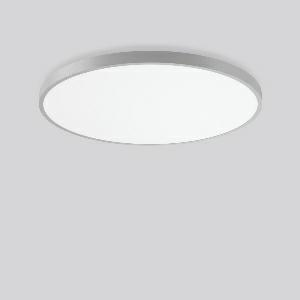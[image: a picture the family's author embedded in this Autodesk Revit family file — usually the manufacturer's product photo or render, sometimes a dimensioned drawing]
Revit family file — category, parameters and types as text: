
# Revit family: triona_round_a_312391_004_730_01d8
name_source: partatom
category: Lighting Fixtures
units: mm (PartAtom-declared; Revit-internal decimal feet)

## family parameters
Cut with Voids When Loaded = No
Host = Face
Light Source = No
Part Type = Normal
Room Calculation Point = No
Round Connector Dimension = Use Diameter
Shared = No

## types (1)
- TRIONA round A (1 x LED Modul 830, 11200 lm, 3000)
    Apparent Load = 106 VA
    CIE Flux Codes = 49 80 96 100 100
    Color Rendering = 80
    Color Temperature = 3000
    Default Elevation = 1800 mm
    Description = Series: TRIONA round
Decorative round LED surface-mounted luminaire. Flat, seamless frame: aluminium extrusion profile, powder coated. Cover made of sheet steel, powder-coated. Light emission through a diffuser: plastic, opal. Lightguide and diffuser made of non-yellowing plastic (PMMA). Lateral light emission (RZB SIDELITE technology) for above-average homogeneous light distribution. Suitable for Ceiling mounting, Wall (surface). Tool-free mounting via bayonet connection. Electronic ballast included. Very easy installation thanks to Plug+Play connection. With Casambi smart+free Bluetooth control for wireless network and operation using Android / iOS devices, free app available for download. 
Colour: silver, matt (approx. RAL 9006)
Diameter: 1009 mm
Height: 88 mm
Lamp: LED
Socket: without socket
Colour temperature: 3000K
Colour rendering index (CRI): 80
System power: 106 W
Rated luminous flux: 11200 lm
Luminous efficiency: 106 lm/W
Control gear: Dimmable Bluetooth converter
Protection class: I
Type of protection: IP 20
    Height = 88 mm
    Lamp = 1 x LED Modul 830
    Lamp Light Flux = 11200 lm
    Lamp count = 1
    Length = 1009 mm
    Lifetime = 50000 h
    Luminous efficacy = 106 lm/W
    Manufacturer = RZB
    ModVariant = No
    Model = 312391.004.730
    Mounting Place = Ceiling
    Mounting Type = Surface mounted
    Number of Poles = 1
    OnlyDefault = Yes
    Power Factor = 1
    Product Name = TRIONA round A
    Product group = Surface mounted modular luminaires
    ProductGroupID = 306
    Protection Class = Protection class I
    Protection Degree = IP 20
    RLX_Detail_Level = 1
    RLX_Emergency_Light_Flux = 0 lm
    RLX_Emergency_Type = 0
    RLX_Emergency_Type_DB = No
    RlxData = <blob elided: 37561 chars, md5=a2ca46f4>
    Socket = socket
    Standby Power = 0 W
    System Light Flux = 11200 lm
    System Power = 106 W
    Type Comments = Product without accessories
    Type Image = 312392.004.jpg
    URL = http://relux.com
    VarID = ---
    Voltage = 230 V
    Voltage Range = 220-240 V
    Weight = 0.00 kg
    Width = 0 mm  [stored 0 ft]

note: [stored X ft] marks values corroborated as IEEE doubles in the binary element streams (Revit-internal decimal feet)

## geometry (parser evidence)
native form markers: Blend x4, Sweep x9
no freeform markers — native parametric forms only
